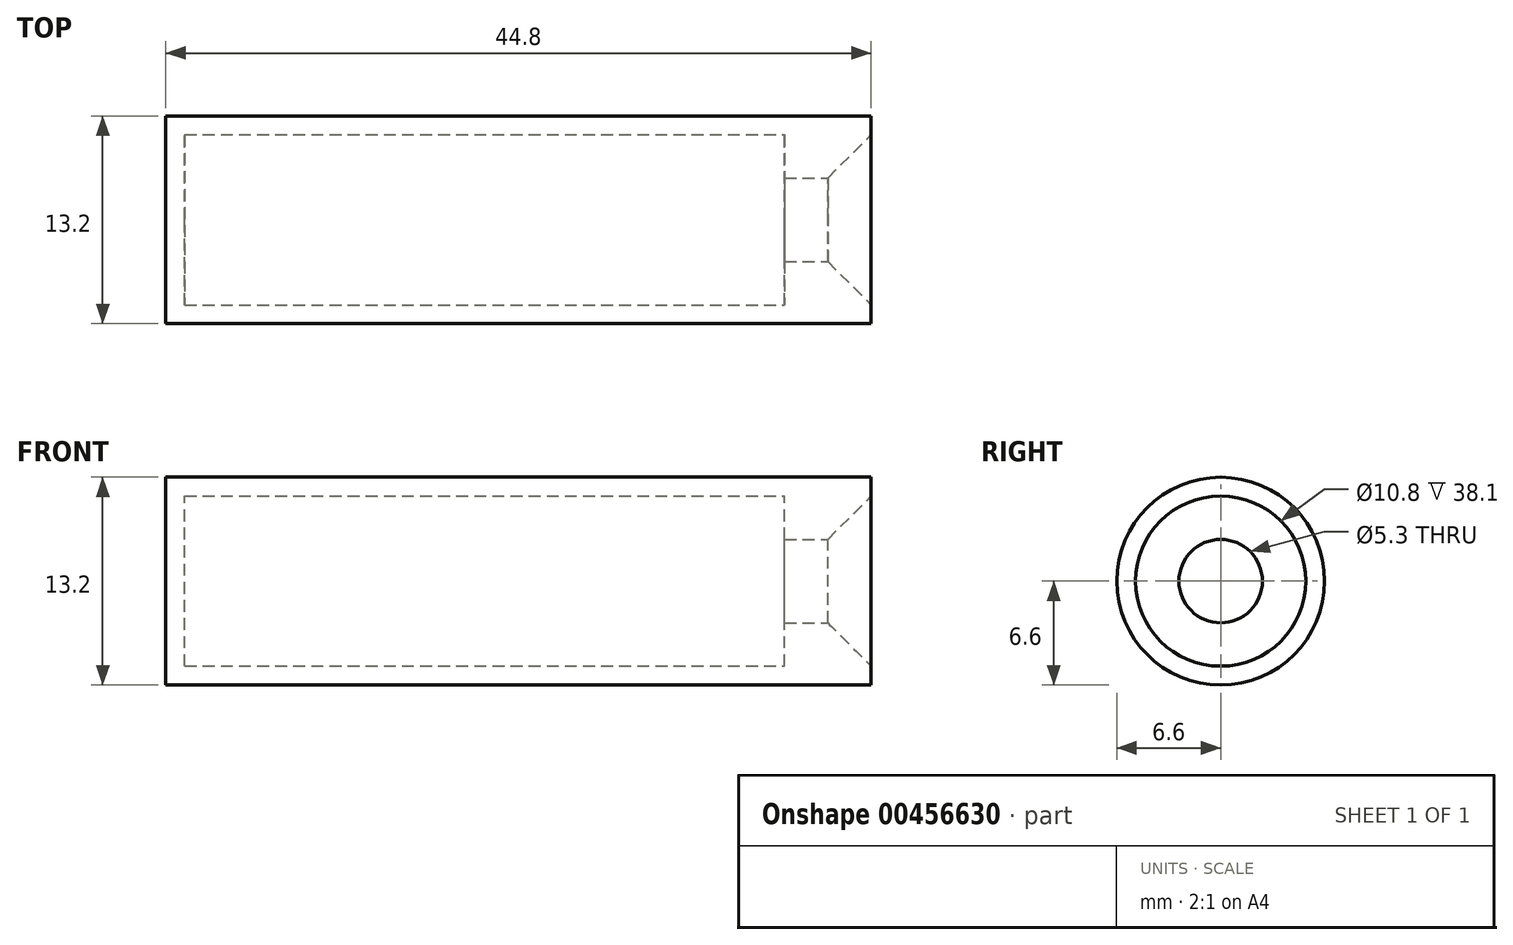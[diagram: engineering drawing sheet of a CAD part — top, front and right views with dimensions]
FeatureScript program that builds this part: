
annotation { "Feature Type Name" : "Feature", "Feature Type Description" : "" }
export const myFeature = defineFeature(function(context is Context, id is Id, definition is map)
    precondition{}
    {
        {
            var Q0;
            Q0=qCreatedBy(makeId("Front.planeOp"),FACE);
            var sketch = newSketch(context, id + "F0", { "sketchPlane" : qUnion([Q0])});
            skLineSegment(sketch, "E0", {"start": v(0, 0) * mm, "end": v(0, 6.6) * mm});
            skLineSegment(sketch, "E1", {"start": v(0, 6.6) * mm, "end": v(44.8, 6.6) * mm});
            skLineSegment(sketch, "E2", {"start": v(44.8, 6.6) * mm, "end": v(44.8, 5.4) * mm});
            skLineSegment(sketch, "E3", {"start": v(39.3, 2.65) * mm, "end": v(39.3, 5.4) * mm});
            skLineSegment(sketch, "E4", {"start": v(39.3, 5.4) * mm, "end": v(1.2, 5.4) * mm});
            skLineSegment(sketch, "E5", {"start": v(1.2, 5.4) * mm, "end": v(1.2, 0) * mm});
            skLineSegment(sketch, "E6", {"start": v(1.2, 0) * mm, "end": v(0, 0) * mm});
            skLineSegment(sketch, "E7", {"start": v(39.3, 2.65) * mm, "end": v(42.05, 2.65) * mm});
            skLineSegment(sketch, "E8", {"start": v(42.05, 2.65) * mm, "end": v(44.8, 5.4) * mm});
            skSolve(sketch);
        }
        {
            var Q0;
            Q0=makeQuery(id+"F0.imprint","IMPRINT",FACE,{"disambiguationData":[TD([[makeQuery(id+"F0.imprint","IMPRINT",EDGE,{"derivedFrom":sQuery(id+"F0.wireOp",EDGE,"E0")}),-1.0]])]});
            var Q1;
            Q1=sQuery(id+"F0.wireOp",EDGE,"E6");
            revolve(context, id + "F1", {"entities" : qUnion([Q0]), "axis" : qUnion([Q1]), "revolveType" : RevolveType.FULL});
        }
    });
